MODEL slx_9e0289cc5443
CONFIG AbsTol = auto
CONFIG EnableMultiTasking = off
CONFIG FixedStep = auto
CONFIG MaxStep = auto
CONFIG MinStep = auto
CONFIG RelTol = 1e-3
CONFIG SampleTimeConstraint = Unconstrained
CONFIG Solver = VariableStepAuto
CONFIG SolverName = VariableStepAuto
CONFIG StartTime = 0.0
CONFIG StopTime = 100
BLOCK [SubSystem] Chart
  ErrorFcn = Stateflow.Translate.translate
  PermitHierarchicalResolution = ExplicitOnly
  Ports = [11, 3, 0, 1]
  RequestExecContextInheritance = off
  SFBlockType = Chart
  TreatAsAtomicUnit = on
BLOCK [Demux] Chart/ Demux 
  Outputs = 1
  Ports = [1, 1]
BLOCK [S-Function] Chart/ SFunction 
  EnableBusSupport = on
  FunctionName = sf_sfun
  PortCounts = [12 4]
  Ports = [12, 4]
  SFcnIsStateOwnerBlock = off
  SFunctionDeploymentMode = off
  Tag = Stateflow S-Function projekt1 3
BLOCK [Terminator] Chart/ Terminator 
BLOCK [Inport] Chart/c1
  IconDisplay = Port number
BLOCK [Inport] Chart/c2
  IconDisplay = Port number
  Port = 2
BLOCK [Inport] Chart/c3
  IconDisplay = Port number
  Port = 3
BLOCK [Inport] Chart/c4
  IconDisplay = Port number
  Port = 4
BLOCK [Inport] Chart/c5
  IconDisplay = Port number
  Port = 5
BLOCK [Inport] Chart/c6
  IconDisplay = Port number
  Port = 6
BLOCK [Inport] Chart/c7
  IconDisplay = Port number
  Port = 7
BLOCK [Inport] Chart/c8
  IconDisplay = Port number
  Port = 8
BLOCK [TriggerPort] Chart/clock
  Ports = [0, 1]
  ShowOutputPort = on
  StatesWhenEnabling = held
  VariantControl = (inherit)
BLOCK [Inport] Chart/d1
  IconDisplay = Port number
  Port = 9
BLOCK [Inport] Chart/d2
  IconDisplay = Port number
  Port = 11
BLOCK [Inport] Chart/d3
  IconDisplay = Port number
  Port = 10
BLOCK [Outport] Chart/distance
  IconDisplay = Port number
BLOCK [Outport] Chart/health
  IconDisplay = Port number
  Port = 2
BLOCK [Outport] Chart/pos
  IconDisplay = Port number
  Port = 3
BLOCK [Reference] Clock  REF=simulink_extras/Flip Flops/Clock
  Ports = [0, 1]
  SourceBlock = simulink_extras/Flip Flops/Clock
  SourceProductBaseCode = SL
  SourceProductName = Simulink
  SourceType = Digital clock
BLOCK [Constant] Constant
BLOCK [Constant] Constant1
  Value = 0
BLOCK [Constant] Constant2
  Value = 0.5
BLOCK [RelationalOperator] GreaterThanOrEqual
  InputSameDT = off
  OutDataTypeStr = boolean
  Ports = [2, 1]
  RndMeth = Simplest
BLOCK [Mux] Mux
  DisplayOption = bar
  Ports = [4, 1]
BLOCK [Reference] Poisson Integer Generator1  REF=commrandsrc3/Poisson Integer
Generator
  Ports = [0, 1]
  SourceBlock = commrandsrc3/Poisson Integer
Generator
  SourceProductBaseCode = CM
  SourceProductName = Communications System Toolbox
  SourceType = Poisson Integer Generator
BLOCK [Scope] Scope
  Floating = off
  NumInputPorts = 1
  Ports = [1]
  ScopeSpecificationString = Simulink.scopes.TimeScopeBlockCfg('CurrentConfiguration', extmgr.ConfigurationSet(extmgr.Configuration('Core','General UI',true),extmgr.Configuration('Core','Source UI',true),extmgr.Configuration('Sources','WiredSimulink',true),extmgr.Configuration('Visuals','Time Domain',true,'SerializedDisplays',{struct('MinYLimReal','-0.19625','MaxYLimReal','1.76625','YLabelReal','','MinYLimMag','0.00000','MaxY...<+1403ch>
BLOCK [Scope] Scope1
  Floating = off
  NumInputPorts = 1
  Ports = [1]
  ScopeSpecificationString = Simulink.scopes.TimeScopeBlockCfg('CurrentConfiguration', extmgr.ConfigurationSet(extmgr.Configuration('Core','General UI',true),extmgr.Configuration('Core','Source UI',true),extmgr.Configuration('Sources','WiredSimulink',true,'DataLoggingVariableName','ScopeData1'),extmgr.Configuration('Visuals','Time Domain',true),extmgr.Configuration('Tools','Plot Navigation',true),extmgr.Configuration('Tools',...<+40ch>
BLOCK [SubSystem] Signal Builder
  ClipboardFcn = sigbuilder_block('clipboard');
  CloseFcn = sigbuilder_block('close');
  ContinueFcn = sigbuilder_block('continue');
  CopyFcn = sigbuilder_block('copy');
  DeleteFcn = sigbuilder_block('delete');
  LoadFcn = sigbuilder_block('load');
  MaskHideContents = on
  ModelCloseFcn = sigbuilder_block('modelClose');
  NameChangeFcn = sigbuilder_block('namechange');
  OpenFcn = sigbuilder_block('open',[437.6 199.2 550.4 400 ]);
  PauseFcn = sigbuilder_block('pause');
  Ports = [0, 8]
  PreSaveFcn = sigbuilder_block('preSave');
  RequestExecContextInheritance = off
  StartFcn = sigbuilder_block('start');
  StopFcn = sigbuilder_block('stop');
  Tag = STV Subsys
BLOCK [Demux] Signal Builder/Demux
  Outputs = 8
  Ports = [1, 8]
  Tag = STV Demux
BLOCK [FromWorkspace] Signal Builder/FromWs
  SampleTime = 0
  Tag = STV FromWs
  VariableName = tuvar
  ZeroCross = on
BLOCK [Outport] Signal Builder/c1
  IconDisplay = Port number
  Tag = STV Outport
BLOCK [Outport] Signal Builder/c2
  IconDisplay = Port number
  Port = 2
  Tag = STV Outport
BLOCK [Outport] Signal Builder/c3
  IconDisplay = Port number
  Port = 3
  Tag = STV Outport
BLOCK [Outport] Signal Builder/c4
  IconDisplay = Port number
  Port = 4
  Tag = STV Outport
BLOCK [Outport] Signal Builder/c5
  IconDisplay = Port number
  Port = 5
  Tag = STV Outport
BLOCK [Outport] Signal Builder/c6
  IconDisplay = Port number
  Port = 6
  Tag = STV Outport
BLOCK [Outport] Signal Builder/c7
  IconDisplay = Port number
  Port = 7
  Tag = STV Outport
BLOCK [Outport] Signal Builder/c8
  IconDisplay = Port number
  Port = 8
  Tag = STV Outport
BLOCK [Switch] Switch
  Criteria = u2 > Threshold
  InputSameDT = off
  SaturateOnIntegerOverflow = off
LINE Chart:1 -> Mux:1
LINE Chart:2 -> Mux:2
LINE Chart:3 -> Mux:3
LINE Clock:1 -> Chart:trigger
LINE Clock:1 -> Mux:4
LINE Constant1:1 -> Switch:3
LINE Constant2:1 -> GreaterThanOrEqual:2
LINE Constant:1 -> Switch:1
LINE GreaterThanOrEqual:1 -> Scope1:1
LINE GreaterThanOrEqual:1 -> Switch:2
LINE Mux:1 -> Scope:1
LINE Poisson Integer Generator1:1 -> GreaterThanOrEqual:1
LINE Signal Builder:1 -> Chart:1
LINE Signal Builder:2 -> Chart:2
LINE Signal Builder:3 -> Chart:3
LINE Signal Builder:4 -> Chart:4
LINE Signal Builder:5 -> Chart:5
LINE Signal Builder:6 -> Chart:6
LINE Signal Builder:7 -> Chart:7
LINE Signal Builder:8 -> Chart:8
LINE Switch:1 -> Chart:10
LINE Switch:1 -> Chart:11
LINE Switch:1 -> Chart:9
CHART Chart states=9 transitions=9
  STATE_LABEL 'M'
  STATE_LABEL 'H\nen:\nt=t+1\np3=rand'
  STATE_LABEL 'P\nen:\nt=t+1'
  STATE_LABEL 'E%eksploracja\nen:\np1=rand\np2=rand\np4=rand\nkierunek = rand\nt=t+1\nif distance < 2*pi\n    if kierunek > 0.15\n        distance = distance + 3.14/4\n    else distance = distance - 3.14/4\n    end\nelse\n    distance = 3.14/4\nend'
  STATE_LABEL 'D'
  STATE_LABEL 'C\nen:\np9=rand'
  STATE_LABEL 'F'
  STATE_LABEL 'W'
  STATE_LABEL 'R\nen:\np5=rand\np7=rand\nt=t+1\n'
